# Revit family: 0053943
name_source: partatom
category: Lighting Fixtures
revit_build: Autodesk Revit 2017 (Build: 20190507_1515(x64)
units: mm (PartAtom-declared; Revit-internal decimal feet)

## family parameters
Cut with Voids When Loaded = No
Host = Face
Light Source = Yes
OmniClass Number = 23.80.70.00
OmniClass Title = Lighting
Part Type = Normal
Room Calculation Point = No
Round Connector Dimension = Use Diameter
Shared = No

## types (2) — shared parameters
Apparent Load = 17 VA
Assembly Code = D5020200
AssetType = Fixed
CLIPH_DIS_SYL = 101 mm
CLIPH_WIDTH_SYL = 10 mm  [stored 0.0328084 ft]
CLIP_CUTOUT_SYL = 19 mm  [stored 0.062336 ft]
CLIP_HOLE_HE_SYL = 9 mm  [stored 0.0295276 ft]
CLIP_HOLE_SYL = 3 mm  [stored 0.00984252 ft]
ClassificationName = Uniclass2015
ClassificationValue = EF_70_80
Color Filter = 16777215
DIF_SYL = 87 mm
Default Elevation = 1219 mm
Dimming Lamp Color Temperature Shift = <None>
DocumentationLiterature = http://www.sylvania-lighting.com
ElectricShockClassification = Class II
Emit Shape Visible in Rendering = No
Emit from Circle Diameter = 610 mm
IfcExportAs = IfcLightFixtureType
IfcExportType = IfcLightFixtureType
ImpactProtectionIndex = IK06
IngressProtection = IP44/20
Keynote = 16500
LUM1_SYL = 103 mm
LUM2_SYL = 113 mm  [stored 0.370735 ft]
Lamp = LED
LampColourRenderingIndex = 80
LampMacAdamStep = 5
LampsType = LED
Manufacturer = Feilo Sylvania
ManufacturerName = Feilo Sylvania
Material = aluminium housing, other diffuser
Material_1_SYL = <By Category>
Material_2_SYL = <By Category>
Material_3_SYL = <By Category>
Material_4_SYL = <By Category>
NominalDepth = 226 mm
NominalHeight = 21 mm
NominalLength = 226 mm
PowerConsumption = 17 W
PowerFactor = 0.9
Tilt Angle = -90.00°
Type Image = <None>
URL = http://www.sylvania-lighting.com
Voltage = 0 V
Weight = 5.57 kg
zero-valued in all types: Cost

## per-type parameters (varying)
| type | Description | LampColourTemperature | LampNominalLuminous | LuminousEfficacy | Model | ModelNumber | ModelReference | Name | Photometric Web File | TypeName |
| 0053939 ST E DWNLGHT FLT 206 SQ IP44 1650 830 D | START eco Downlight Flat IP44 DIM is an integrated LED recessed downlight with separated phase dimmable driver; 17W; 1650Lm; 97Lm/W; 3000K; IP44 rated from the front; 30,000hrs (L70B50). | 3000 K | 1650 lm | 97 lm/W | ST eco Downlight Flat 206 Sq IP44 1650lm 830 DIM | 53939 | ST eco Downlight Flat 206 Sq IP44 1650lm 830 DIM | ST eco Downlight Flat 206 Sq IP44 1650lm 830 DIM | 0053939.ies | ST eco Downlight Flat 206 Sq IP44 1650lm 830 DIM |
| 0053943 ST E DWNLGHT FLT 206 SQ IP44 1700 840 D | START eco Downlight Flat IP44 DIM is an integrated LED recessed downlight with separated phase dimmable driver; 17W; 1700Lm; 100Lm/W; 4000K; IP44 rated from the front; 30,000hrs (L70B50). | 4000 K | 1700 lm | 100 lm/W | ST eco Downlight Flat 206 Sq IP44 1700lm 840 DIM | 0053943 | ST eco Downlight Flat 206 Sq IP44 1700lm 840 DIM | ST eco Downlight Flat 206 Sq IP44 1700lm 840 DIM | 0053943.ies | ST eco Downlight Flat 206 Sq IP44 1700lm 840 DIM |

note: [stored X ft] marks values corroborated as IEEE doubles in the binary element streams (Revit-internal decimal feet)

## geometry (parser evidence)
native form markers: Sweep x2
no freeform markers — native parametric forms only
